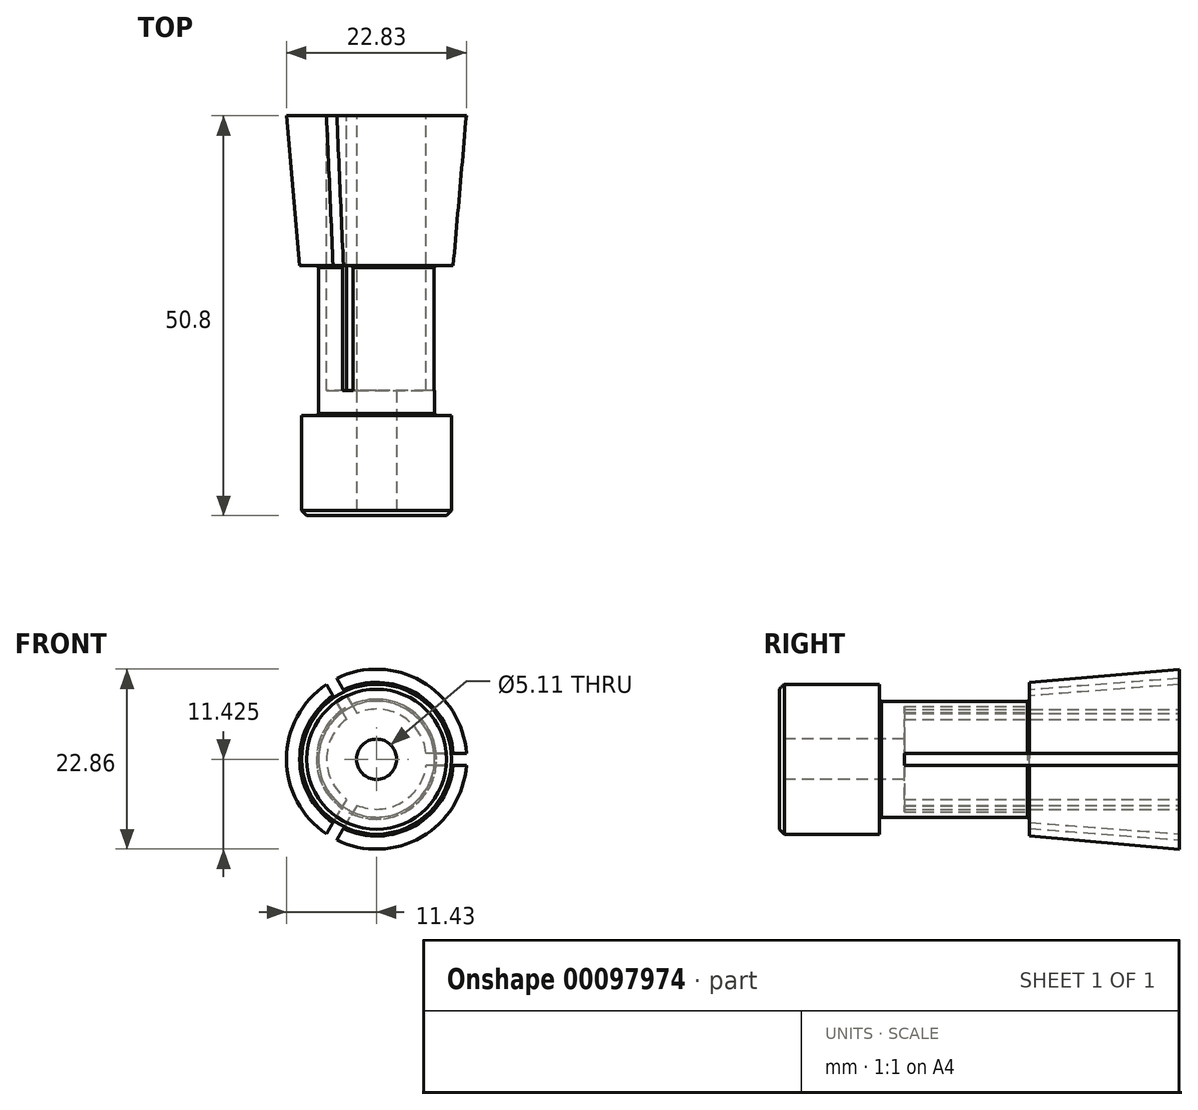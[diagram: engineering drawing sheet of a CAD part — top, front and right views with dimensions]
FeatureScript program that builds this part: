
annotation { "Feature Type Name" : "Feature", "Feature Type Description" : "" }
export const myFeature = defineFeature(function(context is Context, id is Id, definition is map)
    precondition{}
    {
        {
            var Q0;
            Q0=qCreatedBy(makeId("Right.planeOp"),FACE);
            var sketch = newSketch(context, id + "F0", { "sketchPlane" : qUnion([Q0])});
            skLineSegment(sketch, "E0.left", {"start": v(-40.35, 23.77) * mm, "end": v(-40.35, 14.25) * mm});
            skLineSegment(sketch, "E0.right", {"start": v(10.45, 25.68) * mm, "end": v(10.45, 14.25) * mm});
            skLineSegment(sketch, "E1", {"start": v(-40.35, 14.25) * mm, "end": v(10.45, 14.25) * mm});
            skLineSegment(sketch, "E2", {"start": v(-40.35, 23.77) * mm, "end": v(-8.6, 23.77) * mm});
            skLineSegment(sketch, "E3", {"start": v(10.45, 25.68) * mm, "end": v(-11.33, 23.77) * mm});
            skLineSegment(sketch, "E4", {"start": v(-8.6, 24) * mm, "end": v(-8.6, 14.25) * mm, "construction": true});
            skLineSegment(sketch, "E5", {"start": v(-27.65, 23.77) * mm, "end": v(-27.65, 14.25) * mm, "construction": true});
            skPoint(sketch, "E6.orphan", {"position": v(-40.35, 2.82) * mm});
            skPoint(sketch, "E7.orphan", {"position": v(10.45, 4.72) * mm});
            skPoint(sketch, "E8.end.orphan", {"position": v(-11.33, 4.72) * mm});
            skPoint(sketch, "E9.trimOffspring.end.orphan", {"position": v(10.45, 2.82) * mm});
            skPoint(sketch, "E10.orphan", {"position": v(-40.35, 25.68) * mm});
            skPoint(sketch, "E11.orphan", {"position": v(10.45, 23.77) * mm});
            skSolve(sketch);
        }
        {
            var Q0;
            {var subQ1=sQuery(id+"F0.wireOp",EDGE,"E0.left");Q0=makeQuery(id+"F0.imprint","IMPRINT",FACE,{"disambiguationData":[TD([[makeQuery(id+"F0.imprint","IMPRINT",EDGE,{"derivedFrom":subQ1}),1.0]])]});}
            var Q1;
            Q1=sQuery(id+"F0.wireOp",EDGE,"E1");
            revolve(context, id + "F1", {"entities" : qUnion([Q0]), "axis" : qUnion([Q1]), "revolveType" : RevolveType.FULL});
        }
        {
            var Q0;
            Q0=makeQuery(id+"F1.opRevolve","SWEPT_FACE",FACE,{"disambiguationData":[OSD([sQuery(id+"F0.wireOp",EDGE,"E0.right")])]});
            var sketch = newSketch(context, id + "F2", { "sketchPlane" : qUnion([Q0])});
            skCircle(sketch, "E12.0.0", {"center": v(0, 14.25) * mm, "radius": 11.43 * mm, "construction": true});
            skCircle(sketch, "E13", {"center": v(0, 14.25) * mm, "radius": 6.35 * mm});
            skSolve(sketch);
        }
        {
            var Q0;
            Q0=makeQuery(id+"F2.imprint","IMPRINT",FACE,{"disambiguationData":[TD([[makeQuery(id+"F2.imprint","IMPRINT",EDGE,{"derivedFrom":sQuery(id+"F2.wireOp",EDGE,"E13")}),1.0]])]});
            extrude(context, id + "F3", {"entities" : qUnion([Q0]), "operationType" : NewBodyOperationType.REMOVE, "oppositeDirection" : true, "depth" : 34.92 * mm});
        }
        {
            var Q0;
            Q0=makeQuery(id+"F1.opRevolve","SWEPT_FACE",FACE,{"disambiguationData":[OSD([sQuery(id+"F0.wireOp",EDGE,"E0.left")])]});
            var sketch = newSketch(context, id + "F4", { "sketchPlane" : qUnion([Q0])});
            skCircle(sketch, "E14.0.0", {"center": v(0, 14.25) * mm, "radius": 9.52 * mm, "construction": true});
            skSolve(sketch);
        }
        {
            var Q0;
            Q0=sQuery(id+"F4.wireOp",VERTEX,"E14.0.0.center");
            var Q1;
            Q1=makeQuery(id+"F1.opRevolve","SWEPT_BODY",BODY,{"disambiguationData":[OSD([sQuery(id+"F0.wireOp",EDGE,"E0.left"),sQuery(id+"F0.wireOp",EDGE,"E0.right"),sQuery(id+"F0.wireOp",EDGE,"E1"),sQuery(id+"F0.wireOp",EDGE,"E2"),sQuery(id+"F0.wireOp",EDGE,"E3")])]});
            hole(context, id + "F5", {"style" : HoleStyle.SIMPLE, "endStyle" : HoleEndStyle.THROUGH, "standardTappedOrClearance" : lookupTablePath({ "standard" : "ANSI", "engagement" : "75%", "pitch" : "20 tpi", "size" : "1/4", "type" : "Tapped" }), "standardBlindInLast" : lookupTablePath({ "standard" : "ANSI", "engagement" : "75%", "pitch" : "20 tpi", "size" : "1/4", "type" : "Tapped" }), "holeDiameter" : 5.1 * mm, "locations" : qUnion([Q0]), "scope" : qUnion([Q1]), "isTappedThrough" : true, "majorDiameter" : 6.35 * mm, "showTappedDepth" : true});
        }
        {
            var Q0;
            Q0=qCreatedBy(makeId("Right.planeOp"),FACE);
            var sketch = newSketch(context, id + "F6", { "sketchPlane" : qUnion([Q0])});
            skLineSegment(sketch, "E15.0", {"start": v(-27.65, 23.77) * mm, "end": v(-27.65, 21.61) * mm, "construction": true});
            skLineSegment(sketch, "E16.0", {"start": v(-40.35, 14.25) * mm, "end": v(10.45, 14.25) * mm, "construction": true});
            skLineSegment(sketch, "E17.0", {"start": v(-8.6, 24) * mm, "end": v(-8.6, 21.61) * mm, "construction": true});
            skLineSegment(sketch, "E18", {"start": v(-27.65, 23.77) * mm, "end": v(-27.65, 21.61) * mm});
            skLineSegment(sketch, "E19", {"start": v(-8.6, 24) * mm, "end": v(-8.6, 21.61) * mm});
            skLineSegment(sketch, "E20", {"start": v(-27.65, 21.61) * mm, "end": v(-8.6, 21.61) * mm});
            skPoint(sketch, "E21.trimOffspring.end.orphan", {"position": v(-8.6, 14.25) * mm});
            skPoint(sketch, "E22.orphan", {"position": v(-27.65, 14.25) * mm});
            skLineSegment(sketch, "E23.0", {"start": v(-27.65, 23.77) * mm, "end": v(-11.33, 23.77) * mm});
            skLineSegment(sketch, "E24", {"start": v(-11.33, 23.77) * mm, "end": v(-8.6, 24) * mm});
            skPoint(sketch, "E25.orphan", {"position": v(-40.35, 23.77) * mm});
            skSolve(sketch);
        }
        {
            var Q0;
            Q0 = qSketchRegion(id + "F6", true);
            var Q1;
            Q1=sQuery(id+"F0.wireOp",EDGE,"E1");
            revolve(context, id + "F7", {"operationType" : NewBodyOperationType.REMOVE, "entities" : qUnion([Q0]), "axis" : qUnion([Q1]), "revolveType" : RevolveType.FULL, "oppositeDirection" : true});
        }
        {
            var Q0;
            Q0=makeQuery(id+"F1.opRevolve","SWEPT_FACE",FACE,{"disambiguationData":[OSD([sQuery(id+"F0.wireOp",EDGE,"E0.right")])]});
            var sketch = newSketch(context, id + "F8", { "sketchPlane" : qUnion([Q0])});
            skCircle(sketch, "E26.0", {"center": v(0, 14.25) * mm, "radius": 11.43 * mm});
            skCircle(sketch, "E27.0", {"center": v(0, 14.25) * mm, "radius": 6.35 * mm});
            skLineSegment(sketch, "E28", {"start": v(-11.4, 15) * mm, "end": v(11.4, 15) * mm, "construction": true});
            skLineSegment(sketch, "E29", {"start": v(-11.4, 13.48) * mm, "end": v(11.4, 13.48) * mm, "construction": true});
            skLineSegment(sketch, "E30", {"start": v(-11.4, 15) * mm, "end": v(-6.3, 15) * mm});
            skLineSegment(sketch, "E31", {"start": v(-11.4, 13.48) * mm, "end": v(-6.3, 13.48) * mm});
            skLineSegment(sketch, "E32", {"start": v(0, 14.25) * mm, "end": v(-11.4, 14.25) * mm, "construction": true});
            skCircle(sketch, "E33.cCircle", {"center": v(0, 14.25) * mm, "radius": 9.88 * mm, "construction": true});
            skLineSegment(sketch, "E33.0", {"start": v(-5.7, 4.36) * mm, "end": v(-11.4, 14.24) * mm, "construction": true});
            skLineSegment(sketch, "E33.1", {"start": v(-11.4, 14.24) * mm, "end": v(-5.7, 24.12) * mm, "construction": true});
            skLineSegment(sketch, "E33.2", {"start": v(-5.7, 24.12) * mm, "end": v(5.7, 24.13) * mm, "construction": true});
            skLineSegment(sketch, "E33.3", {"start": v(5.7, 24.13) * mm, "end": v(11.4, 14.25) * mm, "construction": true});
            skLineSegment(sketch, "E33.4", {"start": v(11.4, 14.25) * mm, "end": v(5.7, 4.37) * mm, "construction": true});
            skLineSegment(sketch, "E33.5", {"start": v(5.7, 4.37) * mm, "end": v(-5.7, 4.36) * mm, "construction": true});
            skPoint(sketch, "E33.0.midPoint", {"position": v(-8.56, 9.3) * mm});
            skLineSegment(sketch, "E34", {"start": v(5.04, 24.5) * mm, "end": v(-6.36, 4.75) * mm, "construction": true});
            skLineSegment(sketch, "E35", {"start": v(6.36, 23.74) * mm, "end": v(-5.04, 3.99) * mm, "construction": true});
            skLineSegment(sketch, "E36", {"start": v(5.7, 24.13) * mm, "end": v(0, 14.25) * mm, "construction": true});
            skLineSegment(sketch, "E37", {"start": v(0, 14.25) * mm, "end": v(5.7, 4.37) * mm, "construction": true});
            skLineSegment(sketch, "E38", {"start": v(6.36, 4.75) * mm, "end": v(-5.04, 24.5) * mm, "construction": true});
            skLineSegment(sketch, "E39", {"start": v(-6.36, 23.74) * mm, "end": v(5.04, 3.99) * mm, "construction": true});
            skLineSegment(sketch, "E40", {"start": v(5.04, 24.5) * mm, "end": v(2.5, 20.09) * mm});
            skLineSegment(sketch, "E41", {"start": v(6.36, 23.74) * mm, "end": v(3.81, 19.32) * mm});
            skLineSegment(sketch, "E42", {"start": v(3.81, 9.17) * mm, "end": v(6.36, 4.75) * mm});
            skLineSegment(sketch, "E43", {"start": v(2.5, 8.4) * mm, "end": v(5.04, 3.99) * mm});
            skSolve(sketch);
        }
        {
            var Q0;
            {var subQ0=sQuery(id+"F8.wireOp",EDGE,"E30");Q0=makeQuery(id+"F8.imprint","IMPRINT",FACE,{"disambiguationData":[TD([[makeQuery(id+"F8.imprint","IMPRINT",EDGE,{"derivedFrom":subQ0}),-1.0]])]});}
            var Q1;
            {var subQ0=sQuery(id+"F8.wireOp",EDGE,"E40");Q1=makeQuery(id+"F8.imprint","IMPRINT",FACE,{"disambiguationData":[TD([[makeQuery(id+"F8.imprint","IMPRINT",EDGE,{"derivedFrom":subQ0}),1.0]])]});}
            var Q2;
            {var subQ0=sQuery(id+"F8.wireOp",EDGE,"E42");Q2=makeQuery(id+"F8.imprint","IMPRINT",FACE,{"disambiguationData":[TD([[makeQuery(id+"F8.imprint","IMPRINT",EDGE,{"derivedFrom":subQ0}),-1.0]])]});}
            extrude(context, id + "F9", {"entities" : qUnion([Q0, Q1, Q2]), "operationType" : NewBodyOperationType.REMOVE, "oppositeDirection" : true, "depth" : 34.92 * mm});
        }
        {
            var Q0;
            Q0=makeQuery(id+"F1.opRevolve","SWEPT_EDGE",EDGE,{"disambiguationData":[OSD([sQuery(id+"F0.wireOp",EDGE,"E0.left"),sQuery(id+"F0.wireOp",EDGE,"E2")])]});
            chamfer(context, id + "F10", {"entities" : qUnion([Q0]), "width" : 0.64 * mm, "tangentPropagation" : true});
        }
        {
            var Q0;
            Q0=makeQuery(id+"F7.boolean.opBoolean","COPY",EDGE,{"derivedFrom":makeQuery(id+"F7.opRevolve","SWEPT_EDGE",EDGE,{"disambiguationData":[OSD([sQuery(id+"F6.wireOp",EDGE,"E18"),sQuery(id+"F6.wireOp",EDGE,"E23.0")])]})});
            var Q1;
            {var subQ0=sQuery(id+"F6.wireOp",EDGE,"E19");Q1=makeQuery(id+"F9.boolean.opBoolean","SPLIT",EDGE,{"disambiguationData":[TD([makeQuery(id+"F9.opExtrude","SWEPT_FACE",FACE,{"disambiguationData":[OSD([sQuery(id+"F8.wireOp",EDGE,"E30")])]})])],"derivedFrom":makeQuery(id+"F7.boolean.opBoolean","COPY",EDGE,{"derivedFrom":makeQuery(id+"F7.opRevolve","SWEPT_EDGE",EDGE,{"disambiguationData":[OSD([subQ0,sQuery(id+"F6.wireOp",EDGE,"E24")])]})})});}
            var Q2;
            {var subQ0=sQuery(id+"F6.wireOp",EDGE,"E19");Q2=makeQuery(id+"F9.boolean.opBoolean","SPLIT",EDGE,{"disambiguationData":[TD([makeQuery(id+"F9.opExtrude","SWEPT_FACE",FACE,{"disambiguationData":[OSD([sQuery(id+"F8.wireOp",EDGE,"E31")])]})])],"derivedFrom":makeQuery(id+"F7.boolean.opBoolean","COPY",EDGE,{"derivedFrom":makeQuery(id+"F7.opRevolve","SWEPT_EDGE",EDGE,{"disambiguationData":[OSD([subQ0,sQuery(id+"F6.wireOp",EDGE,"E24")])]})})});}
            var Q3;
            {var subQ0=sQuery(id+"F6.wireOp",EDGE,"E19");Q3=makeQuery(id+"F9.boolean.opBoolean","SPLIT",EDGE,{"disambiguationData":[TD([makeQuery(id+"F9.opExtrude","SWEPT_FACE",FACE,{"disambiguationData":[OSD([sQuery(id+"F8.wireOp",EDGE,"E41")])]})])],"derivedFrom":makeQuery(id+"F7.boolean.opBoolean","COPY",EDGE,{"derivedFrom":makeQuery(id+"F7.opRevolve","SWEPT_EDGE",EDGE,{"disambiguationData":[OSD([subQ0,sQuery(id+"F6.wireOp",EDGE,"E24")])]})})});}
            chamfer(context, id + "F11", {"entities" : qUnion([Q0, Q1, Q2, Q3]), "width" : 0.25 * mm, "tangentPropagation" : true});
        }
    });
